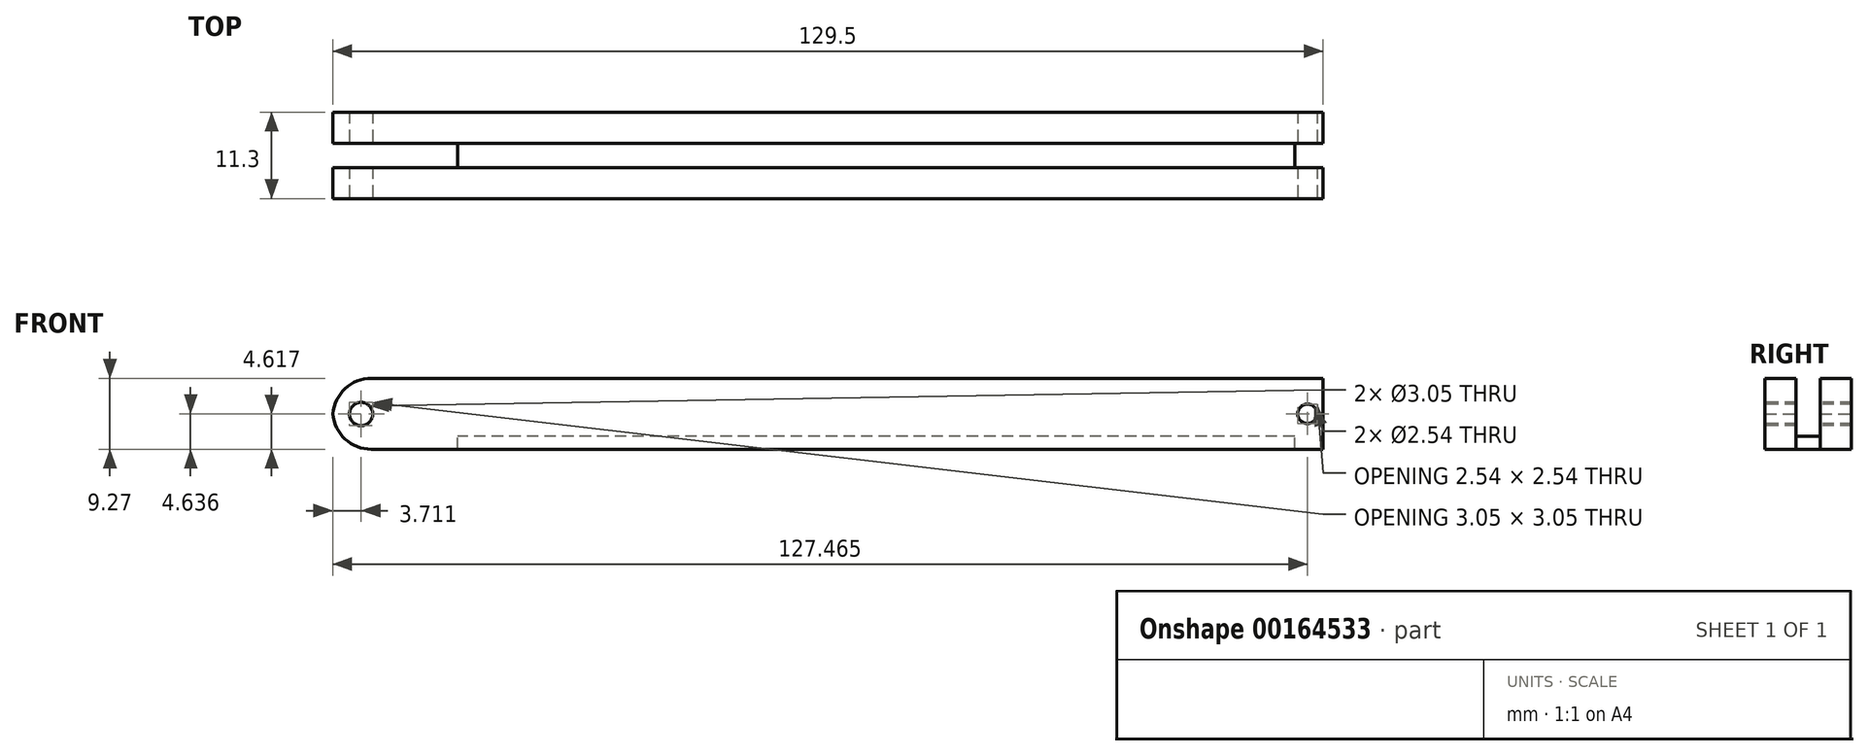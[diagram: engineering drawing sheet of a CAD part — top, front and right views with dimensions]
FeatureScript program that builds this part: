
annotation { "Feature Type Name" : "Feature", "Feature Type Description" : "" }
export const myFeature = defineFeature(function(context is Context, id is Id, definition is map)
    precondition{}
    {
        {
            var Q0;
            Q0=qCreatedBy(makeId("Top.planeOp"),FACE);
            var sketch = newSketch(context, id + "F0", { "sketchPlane" : qUnion([Q0])});
            skLineSegment(sketch, "E0.bottom", {"start": v(64.76, 5.65) * mm, "end": v(-64.76, 5.65) * mm});
            skLineSegment(sketch, "E0.top", {"start": v(64.76, -5.65) * mm, "end": v(-64.76, -5.65) * mm});
            skLineSegment(sketch, "E0.left", {"start": v(64.76, 5.65) * mm, "end": v(64.76, -5.65) * mm});
            skLineSegment(sketch, "E0.right", {"start": v(-64.76, 5.65) * mm, "end": v(-64.76, -5.65) * mm});
            skPoint(sketch, "E0.middle", {"position": v(0, 0) * mm});
            skSolve(sketch);
        }
        {
            var Q0;
            Q0=qSketchRegion(id+"F0",true);
            extrude(context, id + "F1", {"entities" : qUnion([Q0]), "depth" : 9.27 * mm});
        }
        {
            var Q0;
            Q0=makeQuery(id+"F1.opExtrude","CAP_FACE",FACE,{"disambiguationData":[OSD([sQuery(id+"F0.wireOp",EDGE,"E0.bottom"),sQuery(id+"F0.wireOp",EDGE,"E0.top"),sQuery(id+"F0.wireOp",EDGE,"E0.left"),sQuery(id+"F0.wireOp",EDGE,"E0.right")])],"isStart":false});
            var sketch = newSketch(context, id + "F2", { "sketchPlane" : qUnion([Q0])});
            skLineSegment(sketch, "E1.bottom", {"start": v(103.18, -1.59) * mm, "end": v(-103.18, -1.59) * mm});
            skLineSegment(sketch, "E1.top", {"start": v(103.18, 1.59) * mm, "end": v(-103.18, 1.59) * mm});
            skLineSegment(sketch, "E1.left", {"start": v(103.18, -1.59) * mm, "end": v(103.18, 1.59) * mm});
            skLineSegment(sketch, "E1.right", {"start": v(-103.18, -1.59) * mm, "end": v(-103.18, 1.59) * mm});
            skPoint(sketch, "E1.middle", {"position": v(0, 0) * mm});
            skSolve(sketch);
        }
        {
            var Q0;
            Q0=qSketchRegion(id+"F2",true);
            extrude(context, id + "F3", {"entities" : qUnion([Q0]), "operationType" : NewBodyOperationType.REMOVE, "oppositeDirection" : true, "depth" : 7.54 * mm});
        }
        {
            var Q0;
            Q0=makeQuery(id+"F3.boolean.opBoolean","COPY",FACE,{"derivedFrom":makeQuery(id+"F3.opExtrude","CAP_FACE",FACE,{"disambiguationData":[OSD([sQuery(id+"F2.wireOp",EDGE,"E1.bottom"),sQuery(id+"F2.wireOp",EDGE,"E1.top"),sQuery(id+"F2.wireOp",EDGE,"E1.left"),sQuery(id+"F2.wireOp",EDGE,"E1.right")])],"isStart":false})});
            var sketch = newSketch(context, id + "F4", { "sketchPlane" : qUnion([Q0])});
            skLineSegment(sketch, "E2.bottom", {"start": v(64.76, 1.59) * mm, "end": v(61.05, 1.59) * mm});
            skLineSegment(sketch, "E2.top", {"start": v(64.76, -1.59) * mm, "end": v(61.05, -1.59) * mm});
            skLineSegment(sketch, "E2.left", {"start": v(64.76, 1.59) * mm, "end": v(64.76, -1.59) * mm});
            skLineSegment(sketch, "E2.right", {"start": v(61.05, 1.59) * mm, "end": v(61.05, -1.59) * mm});
            skSolve(sketch);
        }
        {
            var Q0;
            Q0=qSketchRegion(id+"F4",true);
            extrude(context, id + "F5", {"entities" : qUnion([Q0]), "operationType" : NewBodyOperationType.REMOVE, "oppositeDirection" : true, "depth" : 25.4 * mm});
        }
        {
            var Q0;
            Q0=makeQuery(id+"F3.boolean.opBoolean","COPY",FACE,{"derivedFrom":makeQuery(id+"F3.opExtrude","CAP_FACE",FACE,{"disambiguationData":[OSD([sQuery(id+"F2.wireOp",EDGE,"E1.bottom"),sQuery(id+"F2.wireOp",EDGE,"E1.top"),sQuery(id+"F2.wireOp",EDGE,"E1.left"),sQuery(id+"F2.wireOp",EDGE,"E1.right")])],"isStart":false})});
            var sketch = newSketch(context, id + "F6", { "sketchPlane" : qUnion([Q0])});
            skLineSegment(sketch, "E3.bottom", {"start": v(-64.76, 1.59) * mm, "end": v(-48.43, 1.59) * mm});
            skLineSegment(sketch, "E3.top", {"start": v(-64.76, -1.59) * mm, "end": v(-48.43, -1.59) * mm});
            skLineSegment(sketch, "E3.left", {"start": v(-64.76, 1.59) * mm, "end": v(-64.76, -1.59) * mm});
            skLineSegment(sketch, "E3.right", {"start": v(-48.43, 1.59) * mm, "end": v(-48.43, -1.59) * mm});
            skSolve(sketch);
        }
        {
            var Q0;
            Q0=qSketchRegion(id+"F6",true);
            extrude(context, id + "F7", {"entities" : qUnion([Q0]), "operationType" : NewBodyOperationType.REMOVE, "oppositeDirection" : true, "depth" : 25.4 * mm});
        }
        {
            var Q0;
            {var subQ0=sQuery(id+"F0.wireOp",EDGE,"E0.right");var subQ1=sQuery(id+"F0.wireOp",EDGE,"E0.top");Q0=makeQuery(id+"F3.boolean.opBoolean","SPLIT",EDGE,{"disambiguationData":[TD([makeQuery(id+"F1.opExtrude","SWEPT_FACE",FACE,{"disambiguationData":[OSD([subQ1])]})])],"derivedFrom":makeQuery(id+"F1.opExtrude","CAP_EDGE",EDGE,{"disambiguationData":[OSD([subQ0])],"isStart":false})});}
            var Q1;
            {var subQ0=sQuery(id+"F0.wireOp",EDGE,"E0.right");var subQ1=sQuery(id+"F0.wireOp",EDGE,"E0.top");Q1=makeQuery(id+"F7.boolean.opBoolean","SPLIT",EDGE,{"disambiguationData":[TD([makeQuery(id+"F1.opExtrude","SWEPT_FACE",FACE,{"disambiguationData":[OSD([subQ1])]})])],"derivedFrom":makeQuery(id+"F1.opExtrude","CAP_EDGE",EDGE,{"disambiguationData":[OSD([subQ0])],"isStart":true})});}
            var Q2;
            {var subQ0=sQuery(id+"F0.wireOp",EDGE,"E0.bottom");var subQ1=sQuery(id+"F0.wireOp",EDGE,"E0.right");Q2=makeQuery(id+"F3.boolean.opBoolean","SPLIT",EDGE,{"disambiguationData":[TD([makeQuery(id+"F1.opExtrude","SWEPT_FACE",FACE,{"disambiguationData":[OSD([subQ0])]})])],"derivedFrom":makeQuery(id+"F1.opExtrude","CAP_EDGE",EDGE,{"disambiguationData":[OSD([subQ1])],"isStart":false})});}
            var Q3;
            {var subQ0=sQuery(id+"F0.wireOp",EDGE,"E0.right");var subQ1=sQuery(id+"F0.wireOp",EDGE,"E0.bottom");Q3=makeQuery(id+"F7.boolean.opBoolean","SPLIT",EDGE,{"disambiguationData":[TD([makeQuery(id+"F1.opExtrude","SWEPT_FACE",FACE,{"disambiguationData":[OSD([subQ1])]})])],"derivedFrom":makeQuery(id+"F1.opExtrude","CAP_EDGE",EDGE,{"disambiguationData":[OSD([subQ0])],"isStart":true})});}
            fillet(context, id + "F8", {"entities" : qUnion([Q0, Q1, Q2, Q3]), "radius" : 5.08 * mm, "tangentPropagation" : true, "allowEdgeOverflow" : false});
        }
        {
            var Q0;
            Q0=makeQuery(id+"F1.opExtrude","SWEPT_FACE",FACE,{"disambiguationData":[OSD([sQuery(id+"F0.wireOp",EDGE,"E0.top")])]});
            var sketch = newSketch(context, id + "F9", { "sketchPlane" : qUnion([Q0])});
            skCircle(sketch, "E4", {"center": v(-61.03, 4.62) * mm, "radius": 1.52 * mm});
            skSolve(sketch);
        }
        {
            var Q0;
            Q0=qSketchRegion(id+"F9",true);
            extrude(context, id + "F10", {"entities" : qUnion([Q0]), "operationType" : NewBodyOperationType.REMOVE, "oppositeDirection" : true, "depth" : 25.4 * mm});
        }
        {
            var Q0;
            Q0=makeQuery(id+"F1.opExtrude","SWEPT_FACE",FACE,{"disambiguationData":[OSD([sQuery(id+"F0.wireOp",EDGE,"E0.top")])]});
            var sketch = newSketch(context, id + "F11", { "sketchPlane" : qUnion([Q0])});
            skCircle(sketch, "E5", {"center": v(62.73, 4.64) * mm, "radius": 1.27 * mm});
            skLineSegment(sketch, "E6", {"start": v(64.76, 4.64) * mm, "end": v(41.42, 4.64) * mm});
            skSolve(sketch);
        }
        {
            var Q0;
            Q0=qSketchRegion(id+"F11",true);
            extrude(context, id + "F12", {"entities" : qUnion([Q0]), "operationType" : NewBodyOperationType.REMOVE, "oppositeDirection" : true, "depth" : 25.4 * mm});
        }
        {
            var Q0;
            Q0=qCreatedBy(makeId("Top.planeOp"),FACE);
            var sketch = newSketch(context, id + "F13", { "sketchPlane" : qUnion([Q0])});
            skLineSegment(sketch, "E7", {"start": v(62.2, -1.23) * mm, "end": v(73.4, -1.23) * mm});
            skLineSegment(sketch, "E8", {"start": v(73.4, -1.23) * mm, "end": v(73.4, 0) * mm});
            skLineSegment(sketch, "E9", {"start": v(73.4, 0) * mm, "end": v(62.2, 0) * mm});
            skLineSegment(sketch, "E10", {"start": v(62.2, 0) * mm, "end": v(62.2, -1.23) * mm});
            skSolve(sketch);
        }
        {
            var Q0;
            Q0 = qSketchRegion(id + "F13", true);
            extrude(context, id + "F14", {"entities" : qUnion([Q0]), "depth" : 4.17 * mm});
        }
        {
            var Q0;
            Q0=makeQuery(id+"F14.opExtrude","SWEPT_FACE",FACE,{"disambiguationData":[OSD([sQuery(id+"F13.wireOp",EDGE,"E8")])]});
            extrude(context, id + "F15", {"entities" : qUnion([Q0]), "depth" : 0.25 * mm});
        }
        {
            var Q0;
            Q0=makeQuery(id+"F15.opExtrude","SWEPT_FACE",FACE,{"disambiguationData":[OSD([sQuery(id+"F13.wireOp",EDGE,"E7"),sQuery(id+"F13.wireOp",EDGE,"E8")])]});
            extrude(context, id + "F16", {"entities" : qUnion([Q0]), "operationType" : NewBodyOperationType.ADD, "depth" : 3.17 * mm});
        }
        {
            var Q0;
            {var subQ0=sQuery(id+"F13.wireOp",EDGE,"E8");var subQ1=sQuery(id+"F13.wireOp",EDGE,"E7");Q0=makeQuery(id+"F16.boolean.opBoolean","MERGE",FACE,{"derivedFrom":[makeQuery(id+"F15.opExtrude","CAP_FACE",FACE,{"disambiguationData":[OSD([subQ0])],"isStart":false}),makeQuery(id+"F16.opExtrude","SWEPT_FACE",FACE,{"disambiguationData":[OSD([subQ1,subQ0]),TDD([makeQuery(id+"F15.opExtrude","CAP_EDGE",EDGE,{"disambiguationData":[OSD([subQ1,subQ0])],"isStart":false})])]})]});}
            var Q1;
            Q1=makeQuery(id+"F15.opExtrude","CAP_EDGE",EDGE,{"disambiguationData":[OSD([sQuery(id+"F13.wireOp",EDGE,"E8"),sQuery(id+"F13.wireOp",EDGE,"E9")])],"isStart":false});
            revolve(context, id + "F17", {"entities" : qUnion([Q0]), "axis" : qUnion([Q1]), "revolveType" : RevolveType.ONE_DIRECTION, "oppositeDirection" : true, "angle" : 90 * degree});
        }
        {
            var Q0;
            Q0=makeQuery(id+"F15.opExtrude","SWEPT_BODY",BODY,{"disambiguationData":[OSD([sQuery(id+"F13.wireOp",EDGE,"E8")])]});
            var Q1;
            Q1=makeQuery(id+"F14.opExtrude","SWEPT_BODY",BODY,{"disambiguationData":[OSD([sQuery(id+"F13.wireOp",EDGE,"E7"),sQuery(id+"F13.wireOp",EDGE,"E8"),sQuery(id+"F13.wireOp",EDGE,"E10"),sQuery(id+"F13.wireOp",EDGE,"E9")])]});
            var Q2;
            Q2=makeQuery(id+"F17.opRevolve","SWEPT_BODY",BODY,{"disambiguationData":[OSD([sQuery(id+"F13.wireOp",EDGE,"E7"),sQuery(id+"F13.wireOp",EDGE,"E8")])]});
            var Q3;
            Q3=qCreatedBy(makeId("Front.planeOp"),FACE);
            mirror(context, id + "F18", {"entities" : qUnion([Q0, Q1, Q2]), "mirrorPlane" : qUnion([Q3])});
        }
        {
            var Q0;
            Q0=makeQuery(id+"F14.opExtrude","SWEPT_BODY",BODY,{"disambiguationData":[OSD([sQuery(id+"F13.wireOp",EDGE,"E7"),sQuery(id+"F13.wireOp",EDGE,"E8"),sQuery(id+"F13.wireOp",EDGE,"E10"),sQuery(id+"F13.wireOp",EDGE,"E9")])]});
            var Q1;
            Q1=makeQuery(id+"F15.opExtrude","SWEPT_BODY",BODY,{"disambiguationData":[OSD([sQuery(id+"F13.wireOp",EDGE,"E8")])]});
            var Q2;
            Q2=makeQuery(id+"F17.opRevolve","SWEPT_BODY",BODY,{"disambiguationData":[OSD([sQuery(id+"F13.wireOp",EDGE,"E7"),sQuery(id+"F13.wireOp",EDGE,"E8")])]});
            var Q3;
            Q3=makeQuery(id+"F18.opPattern","COPY",BODY,{"derivedFrom":makeQuery(id+"F14.opExtrude","SWEPT_BODY",BODY,{"disambiguationData":[OSD([sQuery(id+"F13.wireOp",EDGE,"E7"),sQuery(id+"F13.wireOp",EDGE,"E8"),sQuery(id+"F13.wireOp",EDGE,"E10"),sQuery(id+"F13.wireOp",EDGE,"E9")])]}),"instanceName":"1"});
            var Q4;
            Q4=makeQuery(id+"F18.opPattern","COPY",BODY,{"derivedFrom":makeQuery(id+"F15.opExtrude","SWEPT_BODY",BODY,{"disambiguationData":[OSD([sQuery(id+"F13.wireOp",EDGE,"E8")])]}),"instanceName":"1"});
            var Q5;
            Q5=makeQuery(id+"F18.opPattern","COPY",BODY,{"derivedFrom":makeQuery(id+"F17.opRevolve","SWEPT_BODY",BODY,{"disambiguationData":[OSD([sQuery(id+"F13.wireOp",EDGE,"E7"),sQuery(id+"F13.wireOp",EDGE,"E8")])]}),"instanceName":"1"});
            deleteBodies(context, id + "F19", {"entities" : qUnion([Q0, Q1, Q2, Q3, Q4, Q5])});
        }
    });
